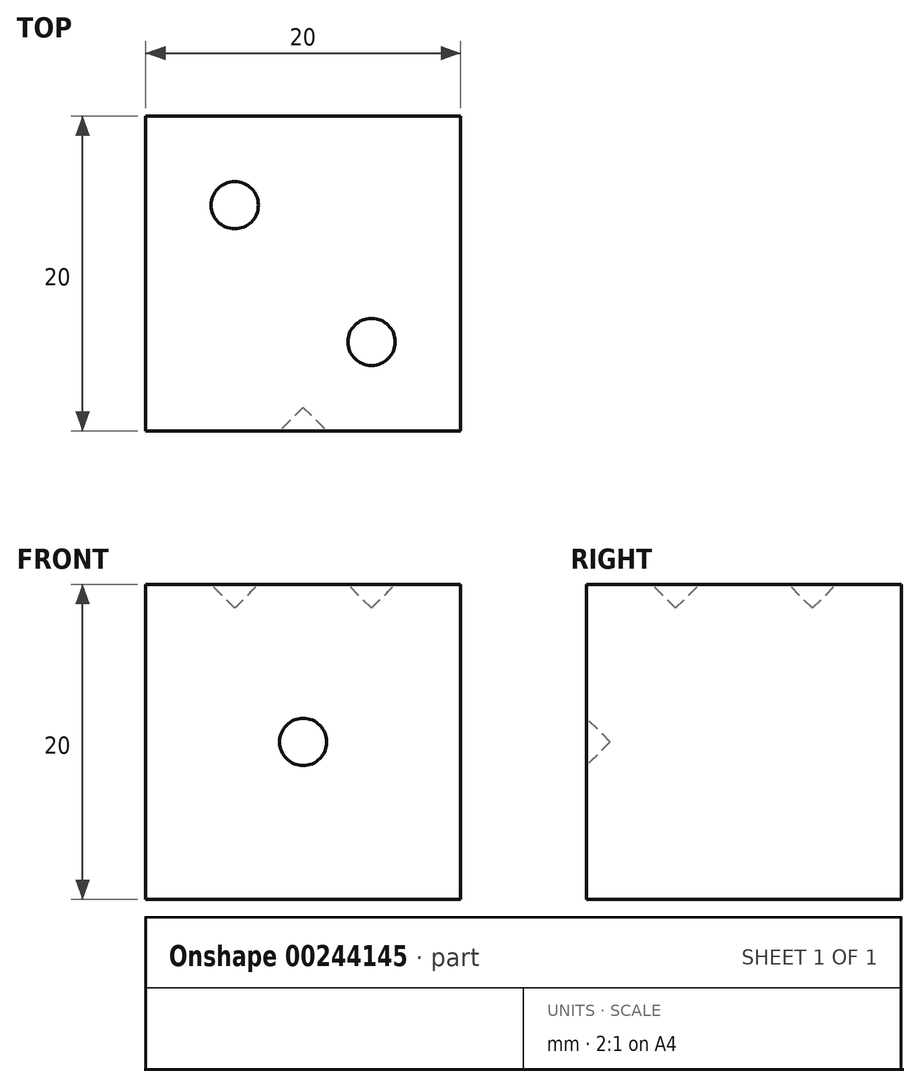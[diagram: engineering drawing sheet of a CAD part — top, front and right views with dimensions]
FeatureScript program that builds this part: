
annotation { "Feature Type Name" : "Feature", "Feature Type Description" : "" }
export const myFeature = defineFeature(function(context is Context, id is Id, definition is map)
    precondition{}
    {
        {
            var Q0;
            Q0=qCreatedBy(makeId("Top.planeOp"),FACE);
            var sketch = newSketch(context, id + "F0", { "sketchPlane" : qUnion([Q0])});
            skLineSegment(sketch, "E0.bottom", {"start": v(0, 0) * mm, "end": v(20, 0) * mm});
            skLineSegment(sketch, "E0.top", {"start": v(0, 20) * mm, "end": v(20, 20) * mm});
            skLineSegment(sketch, "E0.left", {"start": v(0, 0) * mm, "end": v(0, 20) * mm});
            skLineSegment(sketch, "E0.right", {"start": v(20, 0) * mm, "end": v(20, 20) * mm});
            skSolve(sketch);
        }
        {
            var Q0;
            Q0 = qSketchRegion(id + "F0", true);
            extrude(context, id + "F1", {"entities" : qUnion([Q0]), "depth" : 20 * mm});
        }
        {
            var Q0;
            Q0=makeQuery(id+"F1.opExtrude","SWEPT_FACE",FACE,{"disambiguationData":[OSD([sQuery(id+"F0.wireOp",EDGE,"E0.bottom")])]});
            var sketch = newSketch(context, id + "F2", { "sketchPlane" : qUnion([Q0])});
            skLineSegment(sketch, "E1", {"start": v(10, 20) * mm, "end": v(10, 0) * mm, "construction": true});
            skCircle(sketch, "E2", {"center": v(10, 10) * mm, "radius": 1.5 * mm});
            skSolve(sketch);
        }
        {
            var Q0;
            Q0 = qSketchRegion(id + "F2", true);
            extrude(context, id + "F3", {"entities" : qUnion([Q0]), "operationType" : NewBodyOperationType.REMOVE, "oppositeDirection" : true, "depth" : 1.5 * mm});
        }
        {
            var Q0;
            Q0=makeQuery(id+"F1.opExtrude","CAP_FACE",FACE,{"disambiguationData":[OSD([sQuery(id+"F0.wireOp",EDGE,"E0.bottom"),sQuery(id+"F0.wireOp",EDGE,"E0.top"),sQuery(id+"F0.wireOp",EDGE,"E0.left"),sQuery(id+"F0.wireOp",EDGE,"E0.right")])],"isStart":false});
            var sketch = newSketch(context, id + "F4", { "sketchPlane" : qUnion([Q0])});
            skLineSegment(sketch, "E3", {"start": v(0, 20) * mm, "end": v(5.66, 14.34) * mm, "construction": true});
            skLineSegment(sketch, "E4", {"start": v(20, 0) * mm, "end": v(14.34, 5.66) * mm, "construction": true});
            skCircle(sketch, "E5", {"center": v(5.66, 14.34) * mm, "radius": 1.5 * mm});
            skCircle(sketch, "E6", {"center": v(14.34, 5.66) * mm, "radius": 1.5 * mm});
            skSolve(sketch);
        }
        {
            var Q0;
            Q0 = qSketchRegion(id + "F4", true);
            extrude(context, id + "F5", {"entities" : qUnion([Q0]), "operationType" : NewBodyOperationType.REMOVE, "oppositeDirection" : true, "depth" : 1.5 * mm});
        }
        {
            var Q0;
            Q0=makeQuery(id+"F3.boolean.opBoolean","COPY",EDGE,{"derivedFrom":makeQuery(id+"F3.opExtrude","CAP_EDGE",EDGE,{"disambiguationData":[OSD([sQuery(id+"F2.wireOp",EDGE,"E2")])],"isStart":false})});
            var Q1;
            Q1=makeQuery(id+"F5.boolean.opBoolean","COPY",EDGE,{"derivedFrom":makeQuery(id+"F5.opExtrude","CAP_EDGE",EDGE,{"disambiguationData":[OSD([sQuery(id+"F4.wireOp",EDGE,"E5")])],"isStart":false})});
            var Q2;
            Q2=makeQuery(id+"F5.boolean.opBoolean","COPY",EDGE,{"derivedFrom":makeQuery(id+"F5.opExtrude","CAP_EDGE",EDGE,{"disambiguationData":[OSD([sQuery(id+"F4.wireOp",EDGE,"E6")])],"isStart":false})});
            chamfer(context, id + "F6", {"entities" : qUnion([Q0, Q1, Q2]), "width" : 1.5 * mm, "tangentPropagation" : true});
        }
    });
